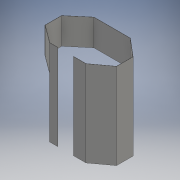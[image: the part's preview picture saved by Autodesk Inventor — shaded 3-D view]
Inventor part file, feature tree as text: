
AUTODESK INVENTOR PART (.ipt)
format: ipt  version: 2016 (Build 200138000, 138)  size: 196,096 bytes
history: native  units: mm
features: sketch x7, extrude x7, plane x1, shell x1
ambient origin geometry x8: Origin, YZ Plane, XZ Plane, XY Plane, X Axis, Y Axis, Z Axis, Center Point
bodies: Body1 (feature_tree)
feature tree (16):
  sketch  "Sketch2"  dims[d19=673.0mm d20=275.5mm d21=251.0mm]
  plane  "Work Plane1"
  extrude  "Extrusion1"  Depth=275.5mm
  shell  "Shell2"  Thickness=251.0mm
  extrude  "Extrusion2"  Depth=331.0mm
  extrude  "Extrusion3"  Depth=534.0mm
  extrude  "Extrusion4"  Depth=3.0mm
  extrude  "Extrusion5"  Depth=3.0mm TaperAngle=0.0deg
  extrude  "Extrusion6"  TaperAngle=180.0deg  [1 undecoded]
  extrude  "Extrusion7"  Depth=3.0mm
  sketch  "Sketch4"  dims[d22=349.0mm d23=331.0mm]
  sketch  "Sketch5"  dims[d24=275.5mm d25=534.0mm]
  sketch  "Sketch6"  dims[d26=200.0mm d44=1306.0mm d45=0.0mm d46=3.0mm]
  sketch  "Sketch7"  dims[d47=3.0mm d48=0.0mm d49=3.0mm d50=0.0mm]
  sketch  "Sketch8"  dims[d51=400.0mm d52=180.0deg]
  sketch  "Sketch9"  dims[d53=816.377mm d54=0.0mm d55=122.0mm d56=900.0mm d57=0.0mm d58=190.0mm d59=900.0mm d60=0.0mm d61=3.0mm d62=0.0mm]
note: 1 required parameter value undecoded (feature->parameter linkage not recoverable at this tier; creation-order binding heuristic only, values carry confidence <= 0.55)
